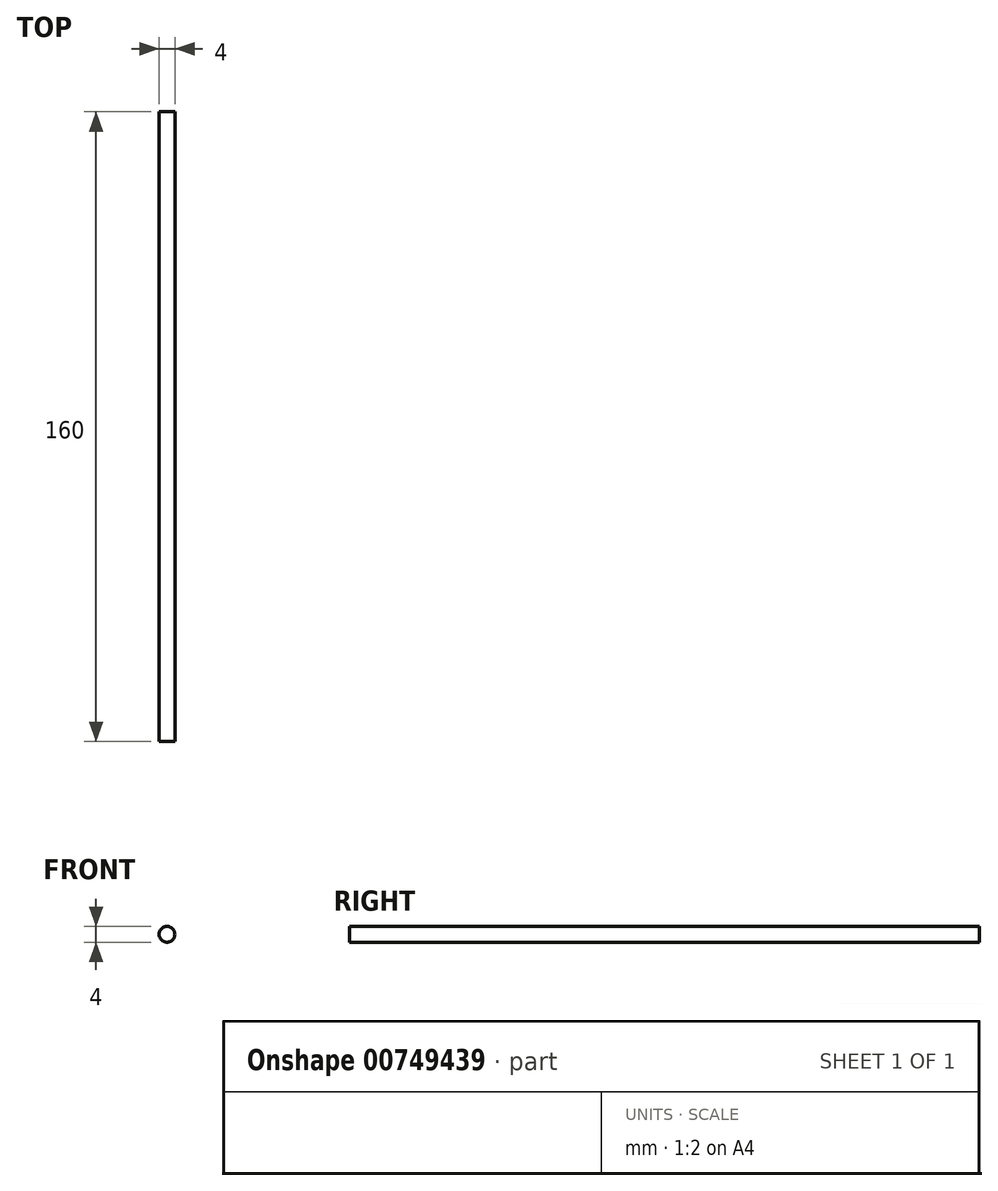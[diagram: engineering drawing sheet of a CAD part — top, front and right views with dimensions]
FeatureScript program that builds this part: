
annotation { "Feature Type Name" : "Feature", "Feature Type Description" : "" }
export const myFeature = defineFeature(function(context is Context, id is Id, definition is map)
    precondition{}
    {
        {
            var Q0;
            Q0=qCreatedBy(makeId("Front.planeOp"),FACE);
            var sketch = newSketch(context, id + "F0", { "sketchPlane" : qUnion([Q0])});
            skCircle(sketch, "E0", {"center": v(-41.8, 0) * mm, "radius": 2 * mm});
            skCircle(sketch, "E1", {"center": v(-27.8, 0) * mm, "radius": 2 * mm});
            skSolve(sketch);
        }
        {
            var Q0;
            Q0=sQuery(id+"F0.wireOp",EDGE,"E0");
            extrude(context, id + "F1", {"bodyType" : ToolBodyType.SURFACE, "surfaceEntities" : qUnion([Q0]), "depth" : 160 * mm, "offsetDistance" : 25 * mm});
        }
    });
